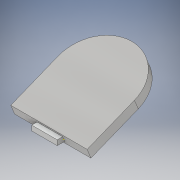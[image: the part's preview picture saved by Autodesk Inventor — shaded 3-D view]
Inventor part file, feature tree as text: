
AUTODESK INVENTOR PART (.ipt)
format: ipt  version: 2018 (Build 220112000, 112)  size: 131,584 bytes
history: native  units: in
note: dims shown in document units (in); Inventor stores cm internally (conversion verified against a paired STEP export)
features: sketch x4, extrude x2, plane x1
ambient origin geometry x8: Origin, YZ Plane, XZ Plane, XY Plane, X Axis, Y Axis, Z Axis, Center Point
bodies: Solid1 (feature_tree)
feature tree (7):
  extrude  "Extrusion1"  Depth=0.7874in
  sketch  "Sketch2"  dims[d2=1.9685in d3=0.0in d4=11.811in]
  plane  "Work Plane1"
  sketch  "Sketch3"  dims[d5=7.874in]
  extrude  "Extrusion2"  Depth=11.811in
  sketch  "Sketch1"  dims[d0=3.937in d1=0.7874in]
  sketch  "Sketch4"  dims[d6=11.811in d7=3.937in d8=0.7676in d9=4.3298in d10=1.5748in d11=0.0in]
